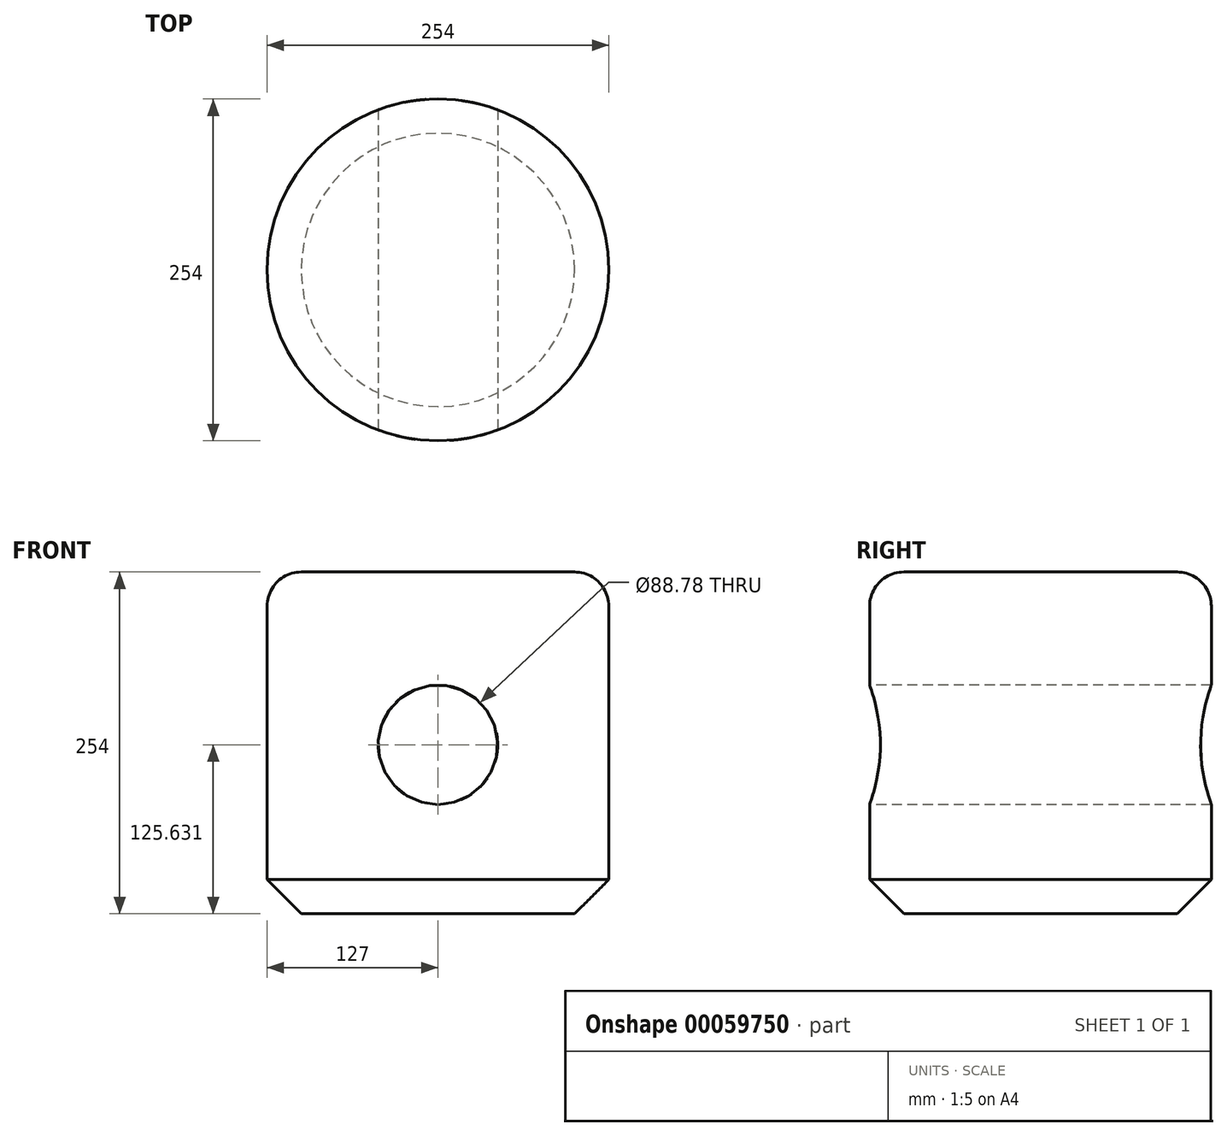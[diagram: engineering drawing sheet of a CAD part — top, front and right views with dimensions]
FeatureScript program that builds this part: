
annotation { "Feature Type Name" : "Feature", "Feature Type Description" : "" }
export const myFeature = defineFeature(function(context is Context, id is Id, definition is map)
    precondition{}
    {
        {
            var Q0;
            Q0=qCreatedBy(makeId("Top.planeOp"),FACE);
            var sketch = newSketch(context, id + "F0", { "sketchPlane" : qUnion([Q0])});
            skCircle(sketch, "E0", {"center": v(0, 0) * mm, "radius": 127 * mm});
            skSolve(sketch);
        }
        {
            var Q0;
            Q0 = qSketchRegion(id + "F0", true);
            extrude(context, id + "F1", {"entities" : qUnion([Q0]), "depth" : 254 * mm});
        }
        {
            var Q0;
            Q0=makeQuery(id+"F1.opExtrude","CAP_EDGE",EDGE,{"disambiguationData":[OSD([sQuery(id+"F0.wireOp",EDGE,"E0")])],"isStart":false});
            fillet(context, id + "F2", {"entities" : qUnion([Q0]), "radius" : 25.4 * mm, "tangentPropagation" : true, "allowEdgeOverflow" : false});
        }
        {
            var Q0;
            Q0=makeQuery(id+"F1.opExtrude","CAP_EDGE",EDGE,{"disambiguationData":[OSD([sQuery(id+"F0.wireOp",EDGE,"E0")])],"isStart":true});
            chamfer(context, id + "F3", {"entities" : qUnion([Q0]), "width" : 25.4 * mm, "tangentPropagation" : true});
        }
        {
            var Q0;
            Q0=qCreatedBy(makeId("Front.planeOp"),FACE);
            var sketch = newSketch(context, id + "F4", { "sketchPlane" : qUnion([Q0])});
            skCircle(sketch, "E1", {"center": v(0, 125.63) * mm, "radius": 44.4 * mm});
            skSolve(sketch);
        }
        {
            var Q0;
            Q0 = qSketchRegion(id + "F4", true);
            extrude(context, id + "F5", {"entities" : qUnion([Q0]), "operationType" : NewBodyOperationType.REMOVE, "endBound" : BoundingType.THROUGH_ALL, "oppositeDirection" : true, "depth" : 250.77 * mm, "hasSecondDirection" : true, "secondDirectionBound" : SecondDirectionBoundingType.THROUGH_ALL, "secondDirectionOppositeDirection" : false, "secondDirectionDepth" : 25 * mm});
        }
    });
